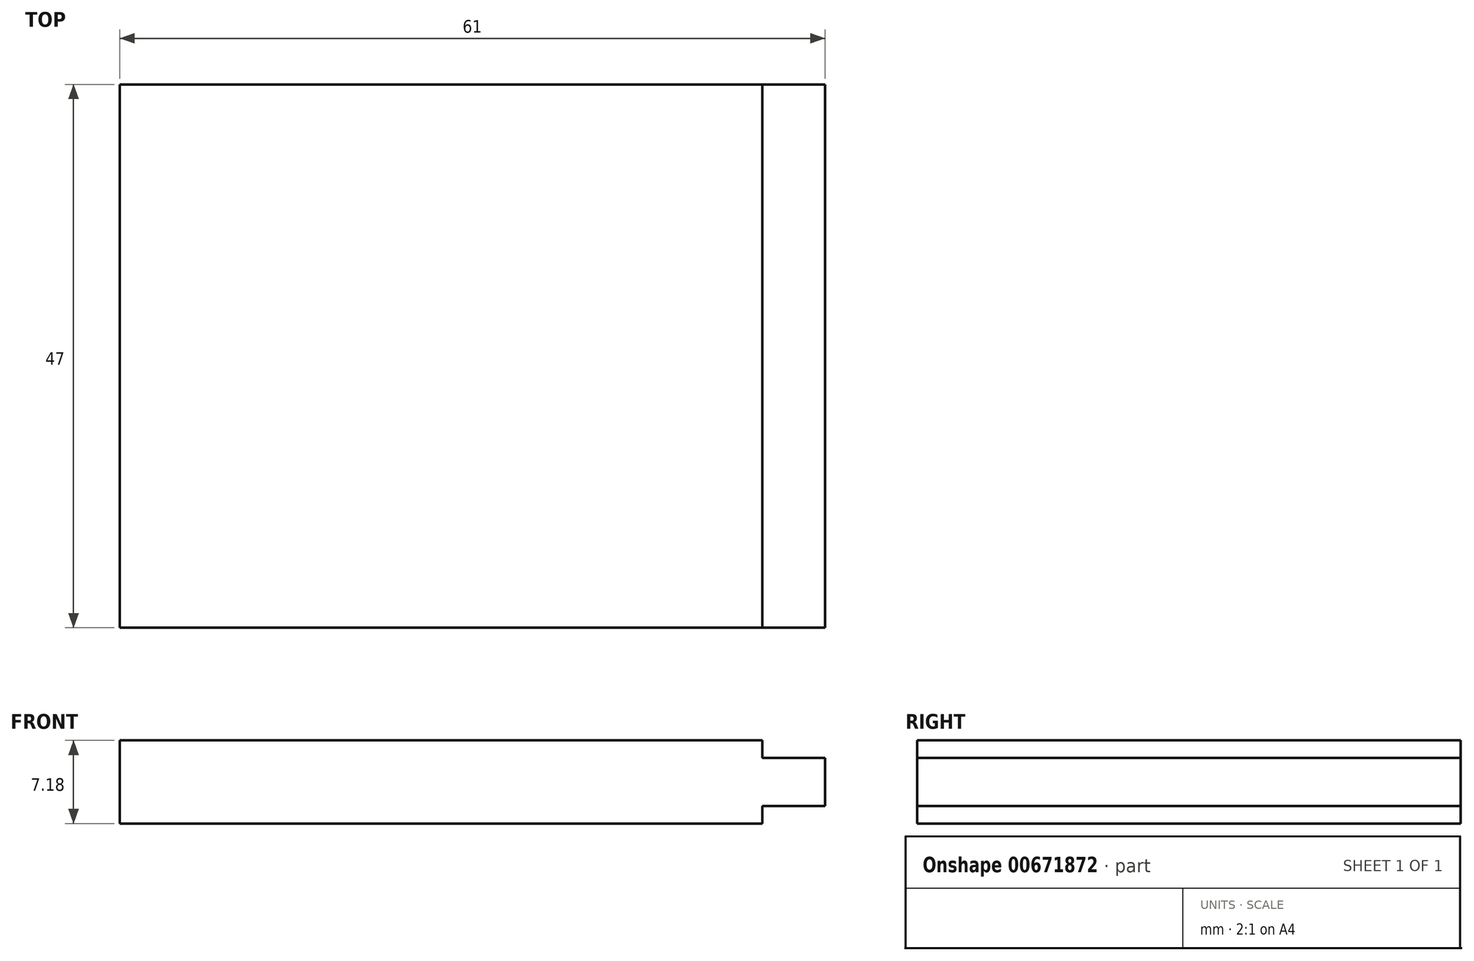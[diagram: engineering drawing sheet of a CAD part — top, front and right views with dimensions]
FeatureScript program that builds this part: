
annotation { "Feature Type Name" : "Feature", "Feature Type Description" : "" }
export const myFeature = defineFeature(function(context is Context, id is Id, definition is map)
    precondition{}
    {
        {
            var Q0;
            Q0=qCreatedBy(makeId("Top.planeOp"),FACE);
            var sketch = newSketch(context, id + "F0", { "sketchPlane" : qUnion([Q0])});
            skLineSegment(sketch, "E0.bottom", {"start": v(30.5, 23.5) * mm, "end": v(-30.5, 23.5) * mm});
            skLineSegment(sketch, "E0.top", {"start": v(30.5, -23.5) * mm, "end": v(-30.5, -23.5) * mm});
            skLineSegment(sketch, "E0.left", {"start": v(30.5, 23.5) * mm, "end": v(30.5, -23.5) * mm});
            skLineSegment(sketch, "E0.right", {"start": v(-30.5, 23.5) * mm, "end": v(-30.5, -23.5) * mm});
            skPoint(sketch, "E0.middle", {"position": v(0, 0) * mm});
            skSolve(sketch);
        }
        {
            var Q0;
            Q0=makeQuery(id+"F0.imprint","IMPRINT",FACE,{"disambiguationData":[TD([[makeQuery(id+"F0.imprint","IMPRINT",EDGE,{"derivedFrom":sQuery(id+"F0.wireOp",EDGE,"E0.bottom")}),1.0]])]});
            extrude(context, id + "F1", {"entities" : qUnion([Q0]), "depth" : 7.18 * mm, "offsetDistance" : 25 * mm});
        }
        {
            var Q0;
            Q0=qCreatedBy(makeId("Front.planeOp"),FACE);
            var sketch = newSketch(context, id + "F2", { "sketchPlane" : qUnion([Q0])});
            skLineSegment(sketch, "E1.0", {"start": v(30.5, 7.18) * mm, "end": v(30.5, 0) * mm});
            skLineSegment(sketch, "E2.bottom", {"start": v(30.5, 7.18) * mm, "end": v(25.1, 7.18) * mm});
            skLineSegment(sketch, "E2.top", {"start": v(30.5, 5.68) * mm, "end": v(25.1, 5.68) * mm});
            skLineSegment(sketch, "E2.left", {"start": v(30.5, 7.18) * mm, "end": v(30.5, 5.68) * mm});
            skLineSegment(sketch, "E2.right", {"start": v(25.1, 7.18) * mm, "end": v(25.1, 5.68) * mm});
            skLineSegment(sketch, "E3.bottom", {"start": v(30.5, 0) * mm, "end": v(25.1, 0) * mm});
            skLineSegment(sketch, "E3.top", {"start": v(30.5, 1.5) * mm, "end": v(25.1, 1.5) * mm});
            skLineSegment(sketch, "E3.left", {"start": v(30.5, 0) * mm, "end": v(30.5, 1.5) * mm});
            skLineSegment(sketch, "E3.right", {"start": v(25.1, 0) * mm, "end": v(25.1, 1.5) * mm});
            skSolve(sketch);
        }
        {
            var Q0;
            Q0 = qSketchRegion(id + "F2", true);
            extrude(context, id + "F3", {"entities" : qUnion([Q0]), "operationType" : NewBodyOperationType.REMOVE, "endBound" : BoundingType.THROUGH_ALL, "oppositeDirection" : true, "depth" : 25 * mm, "offsetDistance" : 25 * mm, "hasSecondDirection" : true, "secondDirectionBound" : SecondDirectionBoundingType.THROUGH_ALL, "secondDirectionOppositeDirection" : false, "secondDirectionDepth" : 25 * mm});
        }
    });
